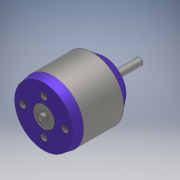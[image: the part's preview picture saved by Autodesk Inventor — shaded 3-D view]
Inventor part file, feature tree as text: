
AUTODESK INVENTOR PART (.ipt)
format: ipt  version: 2017 (Build 210142000, 142)  size: 199,680 bytes
history: native  units: mm
features: sketch x8, extrude x7, thread x5, chamfer x2, revolve x1, pattern_circular x1
ambient origin geometry x8: Origin, YZ Plane, XZ Plane, XY Plane, X Axis, Y Axis, Z Axis, Center Point
bodies: Solid1 (feature_tree)
feature tree (24):
  extrude  "Extrusion1"  Depth=22.0mm TaperAngle=0.0deg
  revolve  "Revolution1"  Angle=90.0deg
  chamfer  "Chamfer1"  Distance=2.0mm
  extrude  "Extrusion2"  Depth=15.82mm TaperAngle=0.0deg
  extrude  "Extrusion3"  Depth=2.0mm TaperAngle=0.0deg
  extrude  "Extrusion4"  Depth=2.0mm
  thread  "Thread1"  [1 undecoded]
  pattern_circular  "Circular Pattern1"  Count=4 Angle=360.0deg
  extrude  "Extrusion5"  Depth=8.0mm
  thread  "Thread2"  [1 undecoded]
  thread  "Thread3"  [1 undecoded]
  thread  "Thread4"  [1 undecoded]
  thread  "Thread5"  [1 undecoded]
  extrude  "Extrusion6"  Depth=10.0mm TaperAngle=0.0deg
  extrude  "Extrusion7"  Depth=10.0mm TaperAngle=0.0deg
  chamfer  "Chamfer2"  Distance=9.5mm
  sketch  "Sketch1"  dims[d0=27.7mm d1=22.0mm d2=0.0mm]
  sketch  "Sketch2"  dims[d3=5.25mm d5=90.0deg]
  sketch  "Sketch3"  dims[d6=9.65mm d7=4.0mm d8=2.0mm d9=1.745329mm]
  sketch  "Sketch4"  dims[d10=3.16mm d11=15.82mm d12=0.0mm]
  sketch  "Sketch5"  dims[d13=8.97mm d14=2.0mm d15=0.0mm]
  sketch  "Sketch6"  dims[d16=6.0mm d17=2.0mm d18=3.0mm d19=0.0mm]
  sketch  "Sketch7"  dims[d20=10.0mm d21=0.0mm d22=40.0mm d23=360.0deg]
  sketch  "Sketch8"  dims[d25=9.5mm d26=8.0mm d27=3.0mm d28=5.0mm d29=0.0mm d30=10.0mm d31=0.0mm d32=10.0mm d33=0.0mm d34=10.0mm d35=0.0mm d36=10.0mm d37=0.0mm d38=9.5mm d39=0.3mm d40=0.0mm d41=2.0mm d42=0.0mm d43=0.2mm d44=2.0mm d45=45.0deg]
note: 5 required parameter values undecoded (feature->parameter linkage not recoverable at this tier; creation-order binding heuristic only, values carry confidence <= 0.55)
